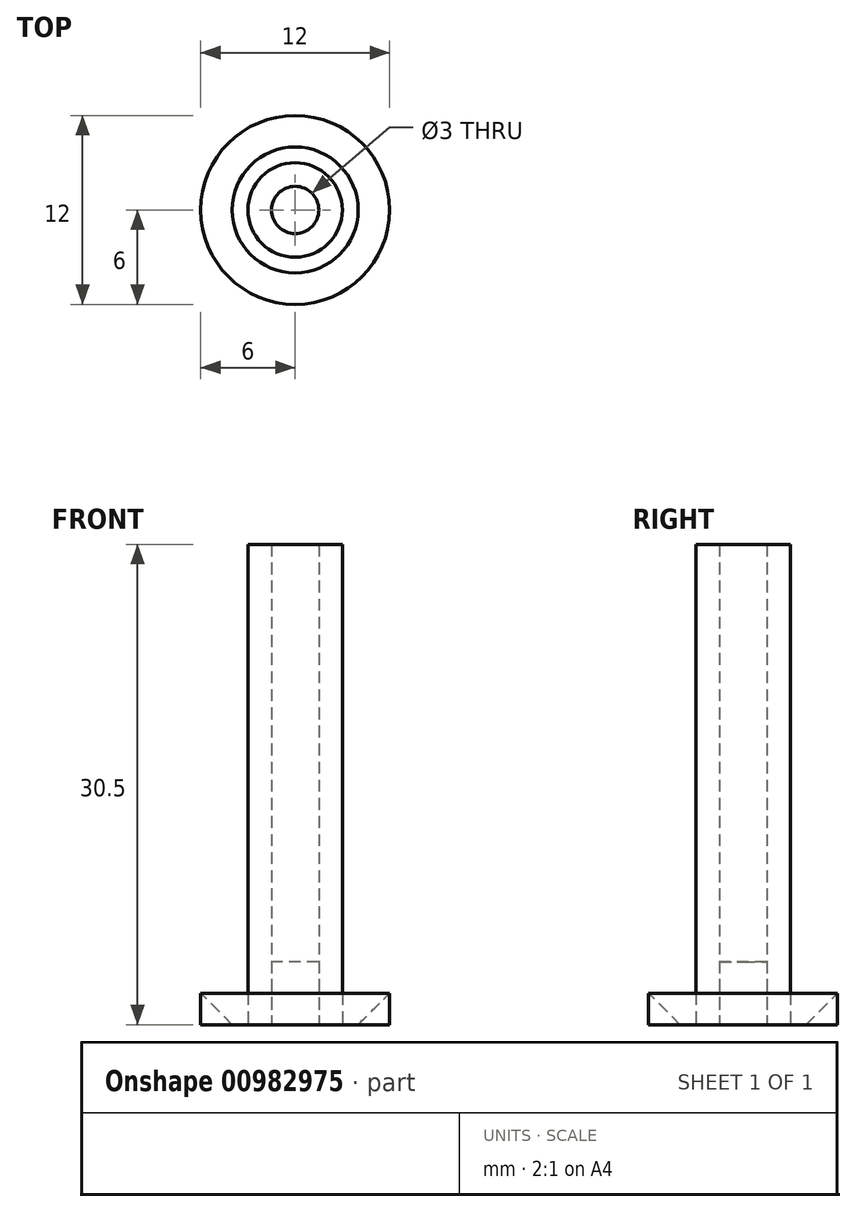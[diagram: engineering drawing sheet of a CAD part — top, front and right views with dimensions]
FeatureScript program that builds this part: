
annotation { "Feature Type Name" : "Feature", "Feature Type Description" : "" }
export const myFeature = defineFeature(function(context is Context, id is Id, definition is map)
    precondition{}
    {
        {
            var Q0;
            Q0=qCreatedBy(makeId("Top.planeOp"),FACE);
            var sketch = newSketch(context, id + "F0", { "sketchPlane" : qUnion([Q0])});
            skCircle(sketch, "E0", {"center": v(0, 0) * mm, "radius": 6 * mm});
            skCircle(sketch, "E1", {"center": v(0, 0) * mm, "radius": 3 * mm});
            skCircle(sketch, "E2", {"center": v(0, 0) * mm, "radius": 1.5 * mm});
            skSolve(sketch);
        }
        {
            var Q0;
            Q0=makeQuery(id+"F0.imprint","IMPRINT",FACE,{"disambiguationData":[TD([[makeQuery(id+"F0.imprint","IMPRINT",EDGE,{"derivedFrom":sQuery(id+"F0.wireOp",EDGE,"E0")}),1.0]])]});
            extrude(context, id + "F1", {"entities" : qUnion([Q0]), "depth" : 2 * mm, "offsetDistance" : 25 * mm});
        }
        {
            var Q0;
            Q0=makeQuery(id+"F0.imprint","IMPRINT",FACE,{"disambiguationData":[TD([[makeQuery(id+"F0.imprint","IMPRINT",EDGE,{"derivedFrom":sQuery(id+"F0.wireOp",EDGE,"E2")}),1.0]])]});
            extrude(context, id + "F2", {"entities" : qUnion([Q0]), "depth" : 4 * mm, "offsetDistance" : 25 * mm});
        }
        {
            assignVariable(context, id + "F3", {"name" : "Aukstis", "anyValue" : 30.5});
        }
        {
            var Q0;
            Q0=makeQuery(id+"F0.imprint","IMPRINT",FACE,{"disambiguationData":[TD([[makeQuery(id+"F0.imprint","IMPRINT",EDGE,{"derivedFrom":sQuery(id+"F0.wireOp",EDGE,"E1")}),1.0]])]});
            extrude(context, id + "F4", {"entities" : qUnion([Q0]), "depth" : (getVariable(context, 'Aukstis')) * mm, "offsetDistance" : 25 * mm});
        }
        {
            var Q0;
            Q0=makeQuery(id+"F1.opExtrude","CAP_EDGE",EDGE,{"disambiguationData":[OSD([sQuery(id+"F0.wireOp",EDGE,"E1")])],"isStart":false});
            chamfer(context, id + "F5", {"entities" : qUnion([Q0]), "width" : 3 * mm, "tangentPropagation" : true});
        }
    });
